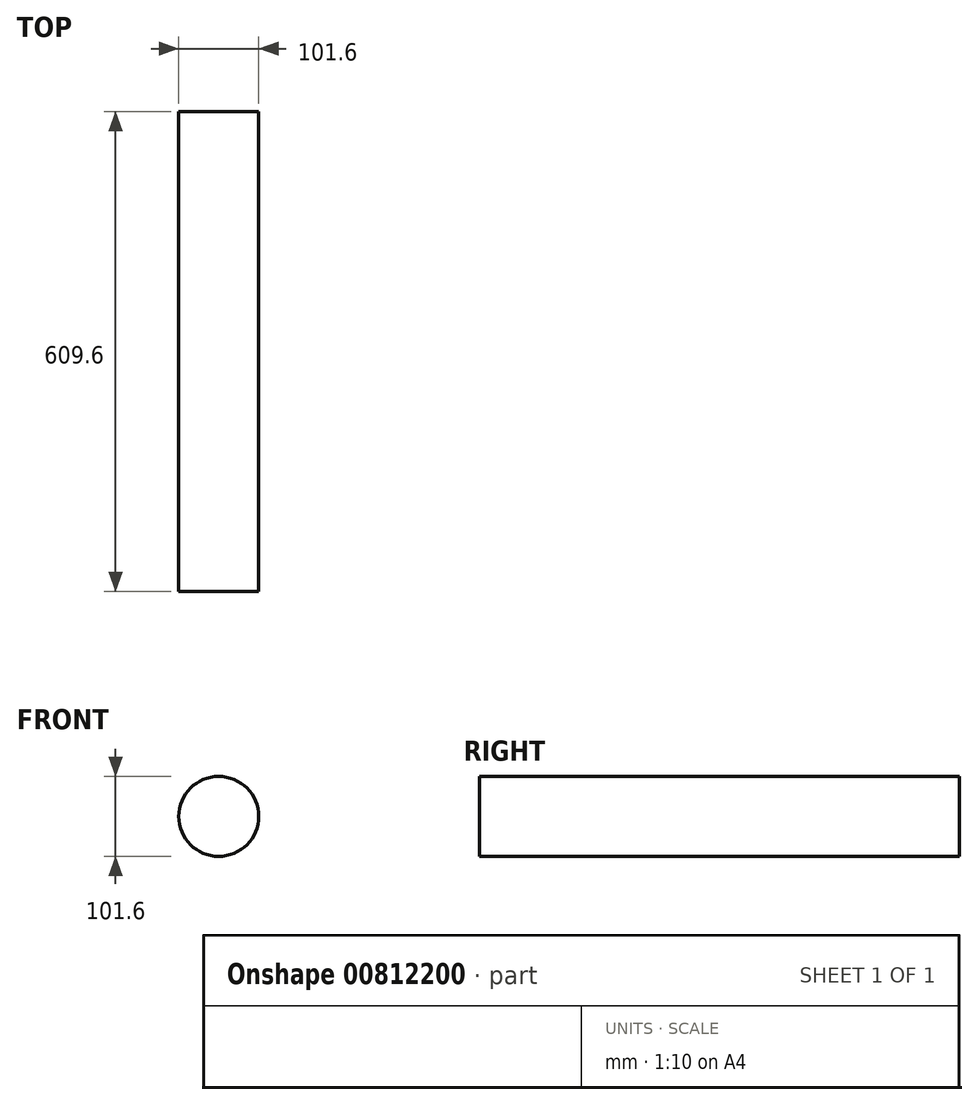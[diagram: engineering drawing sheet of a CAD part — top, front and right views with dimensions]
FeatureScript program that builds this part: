
annotation { "Feature Type Name" : "Feature", "Feature Type Description" : "" }
export const myFeature = defineFeature(function(context is Context, id is Id, definition is map)
    precondition{}
    {
        {
            var Q0;
            Q0=qCreatedBy(makeId("Front.planeOp"),FACE);
            var sketch = newSketch(context, id + "F0", { "sketchPlane" : qUnion([Q0])});
            skCircle(sketch, "E0", {"center": v(0, 0) * mm, "radius": 50.8 * mm});
            skSolve(sketch);
        }
        {
            var Q0;
            Q0=makeQuery(id+"F0.imprint","IMPRINT",FACE,{"disambiguationData":[TD([[makeQuery(id+"F0.imprint","IMPRINT",EDGE,{"derivedFrom":sQuery(id+"F0.wireOp",EDGE,"E0")}),1.0]])]});
            extrude(context, id + "F1", {"entities" : qUnion([Q0]), "depth" : 609.6 * mm, "offsetDistance" : 25.4 * mm});
        }
    });
